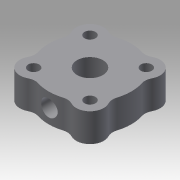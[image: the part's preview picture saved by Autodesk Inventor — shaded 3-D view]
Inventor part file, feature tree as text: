
AUTODESK INVENTOR PART (.ipt)
format: ipt  version: 2016 (Build 200138000, 138)  size: 147,968 bytes
history: native  units: in
note: dims shown in document units (in); Inventor stores cm internally (conversion verified against a paired STEP export)
features: fillet x1
ambient origin geometry x8: Origin, YZ Plane, XZ Plane, XY Plane, X Axis, Y Axis, Z Axis, Center Point
bodies: Solid1 (feature_tree)
feature tree (1):
  fillet  "Fillet1"  [1 undecoded]
note: 1 required parameter value undecoded (feature->parameter linkage not recoverable at this tier; creation-order binding heuristic only, values carry confidence <= 0.55)
